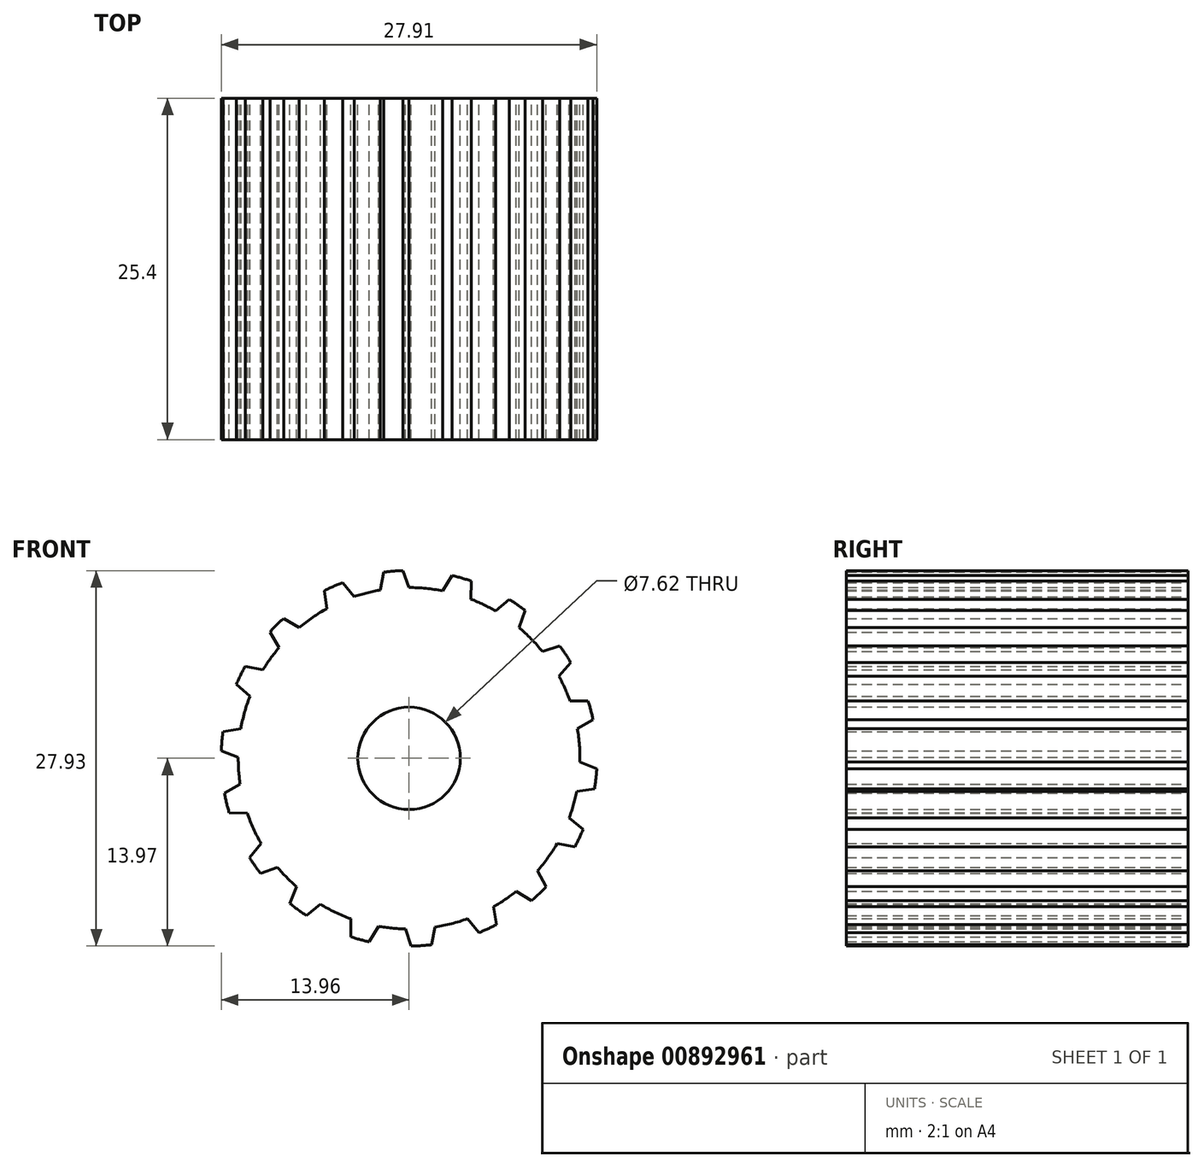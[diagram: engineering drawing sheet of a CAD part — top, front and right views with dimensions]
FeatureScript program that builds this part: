
annotation { "Feature Type Name" : "Feature", "Feature Type Description" : "" }
export const myFeature = defineFeature(function(context is Context, id is Id, definition is map)
    precondition{}
    {
        {
            var Q0;
            Q0=qCreatedBy(makeId("Front.planeOp"),FACE);
            var sketch = newSketch(context, id + "F0", { "sketchPlane" : qUnion([Q0])});
            skCircle(sketch, "E0", {"center": v(0, 0) * mm, "radius": 11.43 * mm, "construction": true});
            skArc(sketch, "E1.0", {"start": v(8.62, 11) * mm, "mid": v(8.05, 11.42) * mm, "end": v(7.45, 11.82) * mm});
            skCircle(sketch, "E2.0", {"center": v(0, 0) * mm, "radius": 12.7 * mm});
            skLineSegment(sketch, "E3", {"start": v(-1.89, 13.84) * mm, "end": v(-2.13, 12.52) * mm});
            skLineSegment(sketch, "E4", {"start": v(-0.46, 13.96) * mm, "end": v(0, 12.7) * mm});
            skPoint(sketch, "E5", {"position": v(-2, 13.18) * mm});
            skPoint(sketch, "E6", {"position": v(-0.23, 13.33) * mm});
            skLineSegment(sketch, "E7", {"start": v(3.18, 13.6) * mm, "end": v(2.49, 12.45) * mm});
            skLineSegment(sketch, "E8", {"start": v(4.63, 13.18) * mm, "end": v(4.6, 11.84) * mm});
            skLineSegment(sketch, "E9", {"start": v(0, 12.7) * mm, "end": v(1.33, 12.7) * mm, "construction": true});
            skLineSegment(sketch, "E10", {"start": v(-1.89, 13.84) * mm, "end": v(-0.46, 13.96) * mm, "construction": true});
            skPoint(sketch, "E11", {"position": v(-1.17, 13.9) * mm});
            skLineSegment(sketch, "E12", {"start": v(3.18, 13.6) * mm, "end": v(4.63, 13.18) * mm, "construction": true});
            skPoint(sketch, "E13", {"position": v(2.84, 13.03) * mm});
            skPoint(sketch, "E14", {"position": v(4.61, 12.5) * mm});
            skPoint(sketch, "E15", {"position": v(3.9, 13.4) * mm});
            skLineSegment(sketch, "E16.1.0", {"start": v(-10.34, 9.4) * mm, "end": v(-9.68, 8.22) * mm});
            skLineSegment(sketch, "E16.1.1", {"start": v(-8.16, 9.73) * mm, "end": v(-7.14, 10.58) * mm, "construction": true});
            skPoint(sketch, "E16.1.2", {"position": v(-10.01, 8.8) * mm});
            skPoint(sketch, "E16.1.3", {"position": v(-4.5, 12.55) * mm});
            skLineSegment(sketch, "E16.1.4", {"start": v(-10.34, 9.4) * mm, "end": v(-9.33, 10.4) * mm, "construction": true});
            skLineSegment(sketch, "E16.1.5", {"start": v(-4.93, 13.07) * mm, "end": v(-4.09, 12.02) * mm});
            skPoint(sketch, "E16.1.6", {"position": v(-8.75, 10.06) * mm});
            skPoint(sketch, "E16.1.7", {"position": v(-5.62, 12.77) * mm});
            skLineSegment(sketch, "E16.1.8", {"start": v(-9.33, 10.4) * mm, "end": v(-8.16, 9.73) * mm});
            skPoint(sketch, "E16.1.9", {"position": v(-9.83, 9.9) * mm});
            skLineSegment(sketch, "E16.1.10", {"start": v(-6.3, 12.47) * mm, "end": v(-4.93, 13.07) * mm, "construction": true});
            skLineSegment(sketch, "E16.1.11", {"start": v(-6.3, 12.47) * mm, "end": v(-6.1, 11.14) * mm});
            skPoint(sketch, "E16.1.12", {"position": v(-6.2, 11.8) * mm});
            skLineSegment(sketch, "E16.2.0", {"start": v(-13.96, 0.55) * mm, "end": v(-12.7, 0.08) * mm});
            skLineSegment(sketch, "E16.2.1", {"start": v(-12.5, 2.2) * mm, "end": v(-12.28, 3.52) * mm, "construction": true});
            skPoint(sketch, "E16.2.2", {"position": v(-13.33, 0.31) * mm});
            skPoint(sketch, "E16.2.3", {"position": v(-11.52, 6.72) * mm});
            skLineSegment(sketch, "E16.2.4", {"start": v(-13.96, 0.55) * mm, "end": v(-13.83, 1.97) * mm, "construction": true});
            skLineSegment(sketch, "E16.2.5", {"start": v(-12.18, 6.85) * mm, "end": v(-10.86, 6.59) * mm});
            skPoint(sketch, "E16.2.6", {"position": v(-13.17, 2.09) * mm});
            skPoint(sketch, "E16.2.7", {"position": v(-12.5, 6.17) * mm});
            skLineSegment(sketch, "E16.2.8", {"start": v(-13.83, 1.97) * mm, "end": v(-12.5, 2.2) * mm});
            skPoint(sketch, "E16.2.9", {"position": v(-13.9, 1.26) * mm});
            skLineSegment(sketch, "E16.2.10", {"start": v(-12.84, 5.5) * mm, "end": v(-12.18, 6.85) * mm, "construction": true});
            skLineSegment(sketch, "E16.2.11", {"start": v(-12.84, 5.5) * mm, "end": v(-11.83, 4.61) * mm});
            skPoint(sketch, "E16.2.12", {"position": v(-12.34, 5.06) * mm});
            skLineSegment(sketch, "E16.3.0", {"start": v(-11.04, -8.56) * mm, "end": v(-9.78, -8.1) * mm});
            skLineSegment(sketch, "E16.3.1", {"start": v(-11, -6.35) * mm, "end": v(-11.66, -5.2) * mm, "construction": true});
            skPoint(sketch, "E16.3.2", {"position": v(-10.41, -8.33) * mm});
            skPoint(sketch, "E16.3.3", {"position": v(-13.14, -2.26) * mm});
            skLineSegment(sketch, "E16.3.4", {"start": v(-11.04, -8.56) * mm, "end": v(-11.86, -7.38) * mm, "construction": true});
            skLineSegment(sketch, "E16.3.5", {"start": v(-13.73, -2.58) * mm, "end": v(-12.55, -1.94) * mm});
            skPoint(sketch, "E16.3.6", {"position": v(-11.43, -6.86) * mm});
            skPoint(sketch, "E16.3.7", {"position": v(-13.55, -3.31) * mm});
            skLineSegment(sketch, "E16.3.8", {"start": v(-11.86, -7.38) * mm, "end": v(-11, -6.35) * mm});
            skPoint(sketch, "E16.3.9", {"position": v(-11.45, -7.97) * mm});
            skLineSegment(sketch, "E16.3.10", {"start": v(-13.37, -4.04) * mm, "end": v(-13.73, -2.58) * mm, "construction": true});
            skLineSegment(sketch, "E16.3.11", {"start": v(-13.37, -4.04) * mm, "end": v(-12.03, -4.07) * mm});
            skPoint(sketch, "E16.3.12", {"position": v(-12.7, -4.06) * mm});
            skLineSegment(sketch, "E16.4.0", {"start": v(-2.96, -13.65) * mm, "end": v(-2.28, -12.5) * mm});
            skLineSegment(sketch, "E16.4.1", {"start": v(-4.34, -11.93) * mm, "end": v(-5.6, -11.48) * mm, "construction": true});
            skPoint(sketch, "E16.4.2", {"position": v(-2.62, -13.07) * mm});
            skPoint(sketch, "E16.4.3", {"position": v(-8.61, -10.18) * mm});
            skLineSegment(sketch, "E16.4.4", {"start": v(-2.96, -13.65) * mm, "end": v(-4.34, -13.28) * mm, "construction": true});
            skLineSegment(sketch, "E16.4.5", {"start": v(-8.86, -10.8) * mm, "end": v(-8.37, -9.55) * mm});
            skPoint(sketch, "E16.4.6", {"position": v(-4.34, -12.6) * mm});
            skPoint(sketch, "E16.4.7", {"position": v(-8.25, -11.25) * mm});
            skLineSegment(sketch, "E16.4.8", {"start": v(-4.34, -13.28) * mm, "end": v(-4.34, -11.93) * mm});
            skPoint(sketch, "E16.4.9", {"position": v(-3.65, -13.47) * mm});
            skLineSegment(sketch, "E16.4.10", {"start": v(-7.65, -11.7) * mm, "end": v(-8.86, -10.8) * mm, "construction": true});
            skLineSegment(sketch, "E16.4.11", {"start": v(-7.65, -11.7) * mm, "end": v(-6.6, -10.85) * mm});
            skPoint(sketch, "E16.4.12", {"position": v(-7.12, -11.27) * mm});
            skLineSegment(sketch, "E16.5.0", {"start": v(6.5, -12.36) * mm, "end": v(6.28, -11.04) * mm});
            skLineSegment(sketch, "E16.5.1", {"start": v(4.34, -11.93) * mm, "end": v(3.1, -12.39) * mm, "construction": true});
            skPoint(sketch, "E16.5.2", {"position": v(6.4, -11.7) * mm});
            skPoint(sketch, "E16.5.3", {"position": v(-0.06, -13.33) * mm});
            skLineSegment(sketch, "E16.5.4", {"start": v(6.5, -12.36) * mm, "end": v(5.2, -12.96) * mm, "construction": true});
            skLineSegment(sketch, "E16.5.5", {"start": v(0.16, -13.97) * mm, "end": v(-0.27, -12.7) * mm});
            skPoint(sketch, "E16.5.6", {"position": v(4.78, -12.45) * mm});
            skPoint(sketch, "E16.5.7", {"position": v(0.9, -13.92) * mm});
            skLineSegment(sketch, "E16.5.8", {"start": v(5.2, -12.96) * mm, "end": v(4.34, -11.93) * mm});
            skPoint(sketch, "E16.5.9", {"position": v(5.86, -12.66) * mm});
            skLineSegment(sketch, "E16.5.10", {"start": v(1.66, -13.87) * mm, "end": v(0.16, -13.97) * mm, "construction": true});
            skLineSegment(sketch, "E16.5.11", {"start": v(1.66, -13.87) * mm, "end": v(1.92, -12.55) * mm});
            skPoint(sketch, "E16.5.12", {"position": v(1.8, -13.21) * mm});
            skLineSegment(sketch, "E16.6.0", {"start": v(12.93, -5.29) * mm, "end": v(11.9, -4.42) * mm});
            skLineSegment(sketch, "E16.6.1", {"start": v(11, -6.35) * mm, "end": v(10.33, -7.5) * mm, "construction": true});
            skPoint(sketch, "E16.6.2", {"position": v(12.42, -4.85) * mm});
            skPoint(sketch, "E16.6.3", {"position": v(8.53, -10.25) * mm});
            skLineSegment(sketch, "E16.6.4", {"start": v(12.93, -5.29) * mm, "end": v(12.32, -6.58) * mm, "construction": true});
            skLineSegment(sketch, "E16.6.5", {"start": v(9.1, -10.6) * mm, "end": v(7.95, -9.9) * mm});
            skPoint(sketch, "E16.6.6", {"position": v(11.66, -6.47) * mm});
            skPoint(sketch, "E16.6.7", {"position": v(9.64, -10.08) * mm});
            skLineSegment(sketch, "E16.6.8", {"start": v(12.32, -6.58) * mm, "end": v(11, -6.35) * mm});
            skPoint(sketch, "E16.6.9", {"position": v(12.63, -5.94) * mm});
            skLineSegment(sketch, "E16.6.10", {"start": v(10.19, -9.56) * mm, "end": v(9.1, -10.6) * mm, "construction": true});
            skLineSegment(sketch, "E16.6.11", {"start": v(10.19, -9.56) * mm, "end": v(9.54, -8.38) * mm});
            skPoint(sketch, "E16.6.12", {"position": v(9.86, -8.97) * mm});
            skLineSegment(sketch, "E16.7.0", {"start": v(13.3, 4.26) * mm, "end": v(11.96, 4.27) * mm});
            skLineSegment(sketch, "E16.7.1", {"start": v(12.5, 2.2) * mm, "end": v(12.74, 0.9) * mm, "construction": true});
            skPoint(sketch, "E16.7.2", {"position": v(12.63, 4.27) * mm});
            skPoint(sketch, "E16.7.3", {"position": v(13.12, -2.37) * mm});
            skLineSegment(sketch, "E16.7.4", {"start": v(13.3, 4.26) * mm, "end": v(13.67, 2.88) * mm, "construction": true});
            skLineSegment(sketch, "E16.7.5", {"start": v(13.78, -2.27) * mm, "end": v(12.46, -2.47) * mm});
            skPoint(sketch, "E16.7.6", {"position": v(13.09, 2.54) * mm});
            skPoint(sketch, "E16.7.7", {"position": v(13.87, -1.52) * mm});
            skLineSegment(sketch, "E16.7.8", {"start": v(13.67, 2.88) * mm, "end": v(12.5, 2.2) * mm});
            skPoint(sketch, "E16.7.9", {"position": v(13.49, 3.57) * mm});
            skLineSegment(sketch, "E16.7.10", {"start": v(13.95, -0.77) * mm, "end": v(13.78, -2.27) * mm, "construction": true});
            skLineSegment(sketch, "E16.7.11", {"start": v(13.95, -0.77) * mm, "end": v(12.7, -0.29) * mm});
            skPoint(sketch, "E16.7.12", {"position": v(13.32, -0.53) * mm});
            skLineSegment(sketch, "E16.8.0", {"start": v(7.45, 11.82) * mm, "end": v(6.42, 10.96) * mm});
            skLineSegment(sketch, "E16.8.1", {"start": v(8.16, 9.73) * mm, "end": v(9.18, 8.87) * mm, "construction": true});
            skPoint(sketch, "E16.8.2", {"position": v(6.93, 11.39) * mm});
            skPoint(sketch, "E16.8.3", {"position": v(11.58, 6.62) * mm});
            skLineSegment(sketch, "E16.8.4", {"start": v(7.45, 11.82) * mm, "end": v(8.62, 11) * mm, "construction": true});
            skLineSegment(sketch, "E16.8.5", {"start": v(12.02, 7.12) * mm, "end": v(11.13, 6.11) * mm});
            skPoint(sketch, "E16.8.6", {"position": v(8.4, 10.36) * mm});
            skPoint(sketch, "E16.8.7", {"position": v(11.6, 7.75) * mm});
            skLineSegment(sketch, "E16.8.8", {"start": v(8.62, 11) * mm, "end": v(8.16, 9.73) * mm});
            skPoint(sketch, "E16.8.9", {"position": v(8.04, 11.4) * mm});
            skLineSegment(sketch, "E16.8.10", {"start": v(11.18, 8.37) * mm, "end": v(12.02, 7.12) * mm, "construction": true});
            skLineSegment(sketch, "E16.8.11", {"start": v(11.18, 8.37) * mm, "end": v(9.91, 7.94) * mm});
            skPoint(sketch, "E16.8.12", {"position": v(10.55, 8.16) * mm});
            skArc(sketch, "E17.trimOffspring", {"start": v(12.02, 7.12) * mm, "mid": v(11.62, 7.76) * mm, "end": v(11.18, 8.37) * mm});
            skArc(sketch, "E18.trimOffspring", {"start": v(13.67, 2.88) * mm, "mid": v(13.5, 3.57) * mm, "end": v(13.3, 4.26) * mm});
            skArc(sketch, "E19.trimOffspring", {"start": v(13.78, -2.27) * mm, "mid": v(13.89, -1.52) * mm, "end": v(13.95, -0.77) * mm});
            skArc(sketch, "E20.trimOffspring", {"start": v(4.63, 13.18) * mm, "mid": v(3.91, 13.41) * mm, "end": v(3.18, 13.6) * mm});
            skArc(sketch, "E21.trimOffspring", {"start": v(-0.46, 13.96) * mm, "mid": v(-1.17, 13.92) * mm, "end": v(-1.89, 13.84) * mm});
            skArc(sketch, "E22.trimOffspring", {"start": v(-4.93, 13.07) * mm, "mid": v(-5.62, 12.79) * mm, "end": v(-6.3, 12.47) * mm});
            skArc(sketch, "E23.trimOffspring", {"start": v(-9.33, 10.4) * mm, "mid": v(-9.85, 9.9) * mm, "end": v(-10.34, 9.4) * mm});
            skArc(sketch, "E24.trimOffspring", {"start": v(-12.18, 6.85) * mm, "mid": v(-12.53, 6.18) * mm, "end": v(-12.84, 5.5) * mm});
            skArc(sketch, "E25.trimOffspring", {"start": v(-13.83, 1.97) * mm, "mid": v(-13.91, 1.26) * mm, "end": v(-13.96, 0.55) * mm});
            skArc(sketch, "E26.trimOffspring", {"start": v(-13.73, -2.58) * mm, "mid": v(-13.57, -3.32) * mm, "end": v(-13.37, -4.04) * mm});
            skArc(sketch, "E27.trimOffspring", {"start": v(-11.86, -7.38) * mm, "mid": v(-11.47, -7.98) * mm, "end": v(-11.04, -8.56) * mm});
            skArc(sketch, "E28.trimOffspring", {"start": v(-8.86, -10.8) * mm, "mid": v(-8.26, -11.26) * mm, "end": v(-7.65, -11.7) * mm});
            skArc(sketch, "E29.trimOffspring", {"start": v(-4.34, -13.28) * mm, "mid": v(-3.66, -13.48) * mm, "end": v(-2.96, -13.65) * mm});
            skArc(sketch, "E30.trimOffspring", {"start": v(0.16, -13.97) * mm, "mid": v(0.91, -13.94) * mm, "end": v(1.66, -13.87) * mm});
            skArc(sketch, "E31.trimOffspring", {"start": v(5.2, -12.96) * mm, "mid": v(5.87, -12.68) * mm, "end": v(6.5, -12.36) * mm});
            skArc(sketch, "E32.trimOffspring", {"start": v(9.1, -10.6) * mm, "mid": v(9.66, -10.1) * mm, "end": v(10.19, -9.56) * mm});
            skArc(sketch, "E33.trimOffspring", {"start": v(12.32, -6.58) * mm, "mid": v(12.64, -5.94) * mm, "end": v(12.93, -5.29) * mm});
            skCircle(sketch, "E34", {"center": v(0, 0) * mm, "radius": 3.81 * mm});
            skSolve(sketch);
        }
        {
            var Q0;
            Q0 = qSketchRegion(id + "F0", true);
            extrude(context, id + "F1", {"entities" : qUnion([Q0]), "depth" : 25.4 * mm, "offsetDistance" : 25.4 * mm});
        }
    });
